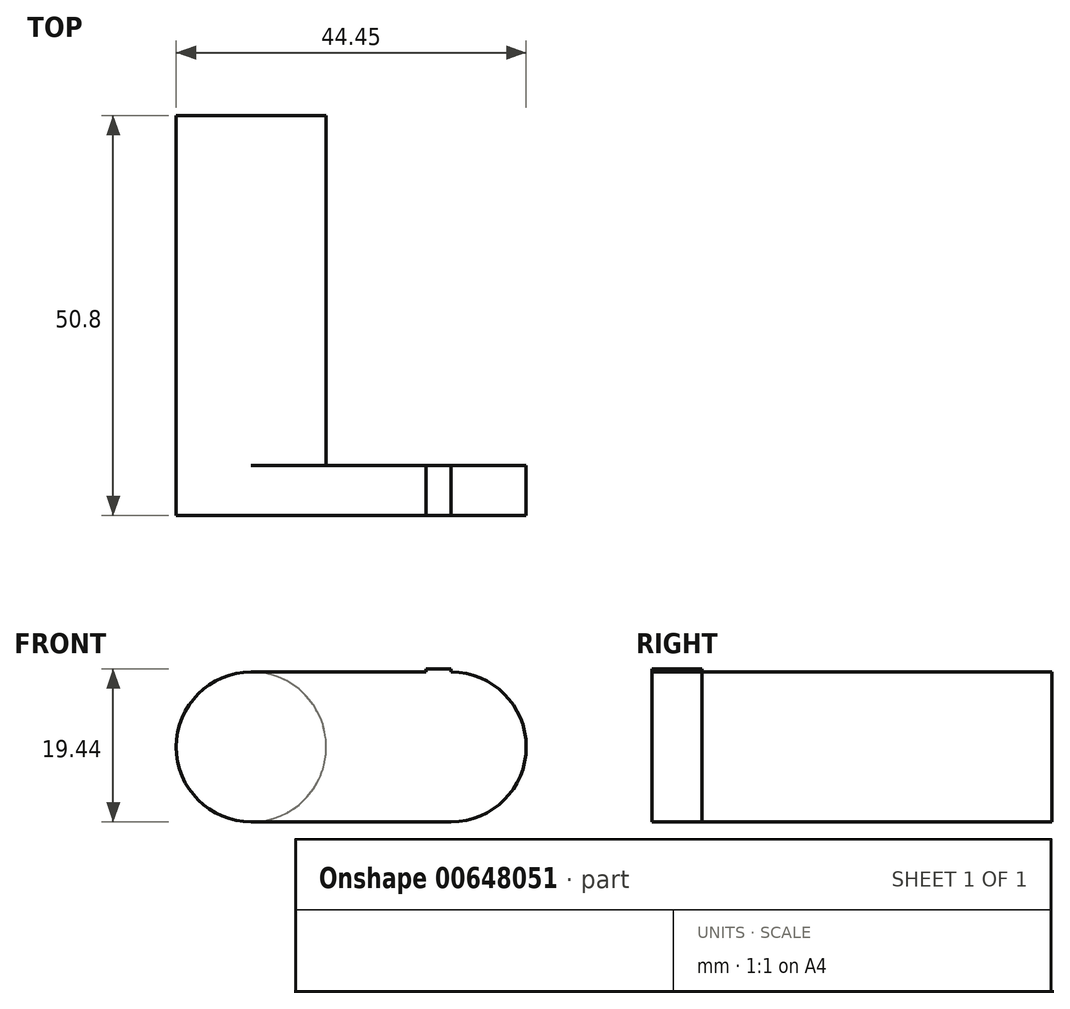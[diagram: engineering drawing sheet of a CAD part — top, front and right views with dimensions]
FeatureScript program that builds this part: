
annotation { "Feature Type Name" : "Feature", "Feature Type Description" : "" }
export const myFeature = defineFeature(function(context is Context, id is Id, definition is map)
    precondition{}
    {
        {
            var Q0;
            Q0=qCreatedBy(makeId("Front.planeOp"),FACE);
            var sketch = newSketch(context, id + "F0", { "sketchPlane" : qUnion([Q0])});
            skCircle(sketch, "E0", {"center": v(0, 0) * mm, "radius": 9.52 * mm});
            skSolve(sketch);
        }
        {
            var Q0;
            Q0 = qSketchRegion(id + "F0", true);
            extrude(context, id + "F1", {"entities" : qUnion([Q0]), "depth" : 50.8 * mm, "offsetDistance" : 25.4 * mm});
        }
        {
            var Q0;
            Q0=makeQuery(id+"F1.opExtrude","CAP_FACE",FACE,{"disambiguationData":[OSD([sQuery(id+"F0.wireOp",EDGE,"E0")])],"isStart":false});
            var sketch = newSketch(context, id + "F2", { "sketchPlane" : qUnion([Q0])});
            skArc(sketch, "E1", {"start": v(25.4, -9.52) * mm, "mid": v(34.92, 0) * mm, "end": v(25.4, 9.52) * mm});
            skArc(sketch, "E2", {"start": v(0, -9.52) * mm, "mid": v(9.52, 0) * mm, "end": v(0, 9.52) * mm});
            skLineSegment(sketch, "E3", {"start": v(0, 9.52) * mm, "end": v(25.4, 9.52) * mm});
            skLineSegment(sketch, "E4", {"start": v(0, -9.52) * mm, "end": v(25.4, -9.52) * mm});
            skSolve(sketch);
        }
        {
            var Q0;
            Q0 = qSketchRegion(id + "F2", true);
            extrude(context, id + "F3", {"entities" : qUnion([Q0]), "operationType" : NewBodyOperationType.ADD, "oppositeDirection" : true, "depth" : 6.35 * mm, "offsetDistance" : 25.4 * mm});
        }
        {
            var Q0;
            Q0=makeQuery(id+"F3.opExtrude","SWEPT_FACE",FACE,{"disambiguationData":[OSD([sQuery(id+"F2.wireOp",EDGE,"E3")])]});
            var sketch = newSketch(context, id + "F4", { "sketchPlane" : qUnion([Q0])});
            skLineSegment(sketch, "E5", {"start": v(25.4, -44.45) * mm, "end": v(25.4, -50.8) * mm});
            skLineSegment(sketch, "E6", {"start": v(25.4, -50.8) * mm, "end": v(22.23, -50.8) * mm});
            skLineSegment(sketch, "E7", {"start": v(22.23, -50.8) * mm, "end": v(22.23, -44.45) * mm});
            skLineSegment(sketch, "E8", {"start": v(22.23, -44.45) * mm, "end": v(25.4, -44.45) * mm});
            skSolve(sketch);
        }
        {
            var Q0;
            Q0 = qSketchRegion(id + "F4", true);
            extrude(context, id + "F5", {"entities" : qUnion([Q0]), "operationType" : NewBodyOperationType.ADD, "depth" : 0.38 * mm, "offsetDistance" : 25.4 * mm});
        }
    });
